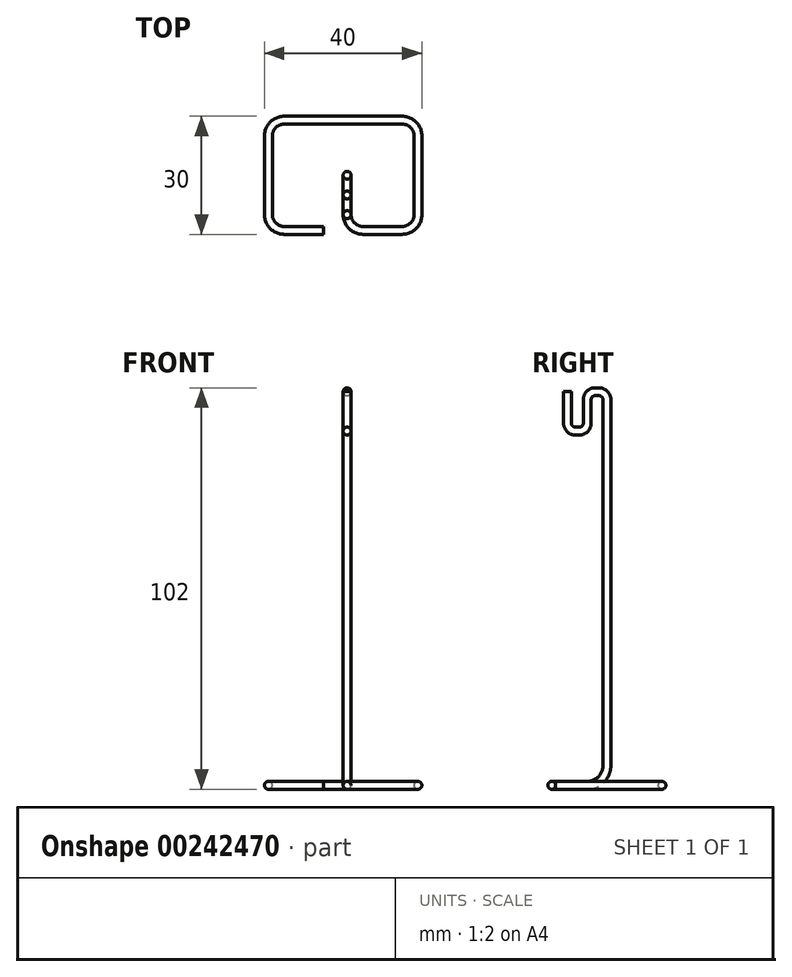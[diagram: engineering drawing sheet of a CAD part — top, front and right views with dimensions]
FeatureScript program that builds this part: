
annotation { "Feature Type Name" : "Feature", "Feature Type Description" : "" }
export const myFeature = defineFeature(function(context is Context, id is Id, definition is map)
    precondition{}
    {
        {
            var Q0;
            Q0=qCreatedBy(makeId("Right.planeOp"),FACE);
            var sketch = newSketch(context, id + "F0", { "sketchPlane" : qUnion([Q0])});
            skLineSegment(sketch, "E0", {"start": v(0, 0) * mm, "end": v(0, 0) * mm});
            skLineSegment(sketch, "E1", {"start": v(5, 5) * mm, "end": v(5, 98) * mm});
            skLineSegment(sketch, "E2", {"start": v(3, 100) * mm, "end": v(2, 100) * mm});
            skLineSegment(sketch, "E3", {"start": v(0, 98) * mm, "end": v(0, 92) * mm});
            skLineSegment(sketch, "E4", {"start": v(-2, 90) * mm, "end": v(-3, 90) * mm});
            skLineSegment(sketch, "E5", {"start": v(-5, 92) * mm, "end": v(-5, 100) * mm});
            skPoint(sketch, "E6.visualSharp", {"position": v(-5, 90) * mm});
            skArc(sketch, "E6.filletArc", {"start": v(-5, 92) * mm, "mid": v(-4.41, 90.59) * mm, "end": v(-3, 90) * mm});
            skPoint(sketch, "E7.visualSharp", {"position": v(0, 90) * mm});
            skArc(sketch, "E7.filletArc", {"start": v(-2, 90) * mm, "mid": v(-0.59, 90.59) * mm, "end": v(0, 92) * mm});
            skPoint(sketch, "E8.visualSharp", {"position": v(0, 100) * mm});
            skArc(sketch, "E8.filletArc", {"start": v(2, 100) * mm, "mid": v(0.59, 99.41) * mm, "end": v(0, 98) * mm});
            skPoint(sketch, "E9.visualSharp", {"position": v(5, 100) * mm});
            skArc(sketch, "E9.filletArc", {"start": v(5, 98) * mm, "mid": v(4.41, 99.41) * mm, "end": v(3, 100) * mm});
            skPoint(sketch, "E10.visualSharp", {"position": v(5, 0) * mm});
            skArc(sketch, "E10.filletArc", {"start": v(0, 0) * mm, "mid": v(3.54, 1.46) * mm, "end": v(5, 5) * mm});
            skPoint(sketch, "E11", {"position": v(-5, 100) * mm});
            skSolve(sketch);
        }
        {
            var Q0;
            Q0=qCreatedBy(makeId("Front.planeOp"),FACE);
            var sketch = newSketch(context, id + "F1", { "sketchPlane" : qUnion([Q0])});
            skCircle(sketch, "E12", {"center": v(1, 0) * mm, "radius": 1 * mm});
            skSolve(sketch);
        }
        {
            var Q0;
            Q0=qCreatedBy(makeId("Top.planeOp"),FACE);
            var sketch = newSketch(context, id + "F2", { "sketchPlane" : qUnion([Q0])});
            skLineSegment(sketch, "E13", {"start": v(0, 0) * mm, "end": v(0, -5) * mm});
            skLineSegment(sketch, "E14", {"start": v(5, -10) * mm, "end": v(15, -10) * mm});
            skLineSegment(sketch, "E15", {"start": v(20, -5) * mm, "end": v(20, 15) * mm});
            skLineSegment(sketch, "E16", {"start": v(15, 20) * mm, "end": v(-15, 20) * mm});
            skLineSegment(sketch, "E17", {"start": v(-20, 15) * mm, "end": v(-20, -5) * mm});
            skLineSegment(sketch, "E18", {"start": v(-15, -10) * mm, "end": v(-5, -10) * mm});
            skPoint(sketch, "E19.visualSharp", {"position": v(-20, -10) * mm});
            skArc(sketch, "E19.filletArc", {"start": v(-20, -5) * mm, "mid": v(-18.54, -8.54) * mm, "end": v(-15, -10) * mm});
            skPoint(sketch, "E20.visualSharp", {"position": v(20, -10) * mm});
            skArc(sketch, "E20.filletArc", {"start": v(15, -10) * mm, "mid": v(18.54, -8.54) * mm, "end": v(20, -5) * mm});
            skPoint(sketch, "E21.visualSharp", {"position": v(20, 20) * mm});
            skArc(sketch, "E21.filletArc", {"start": v(20, 15) * mm, "mid": v(18.54, 18.54) * mm, "end": v(15, 20) * mm});
            skPoint(sketch, "E22.visualSharp", {"position": v(-20, 20) * mm});
            skArc(sketch, "E22.filletArc", {"start": v(-15, 20) * mm, "mid": v(-18.54, 18.54) * mm, "end": v(-20, 15) * mm});
            skPoint(sketch, "E23.visualSharp", {"position": v(0, -10) * mm});
            skArc(sketch, "E23.filletArc", {"start": v(0, -5) * mm, "mid": v(1.46, -8.54) * mm, "end": v(5, -10) * mm});
            skSolve(sketch);
        }
        {
            var Q0;
            Q0=makeQuery(id+"F1.imprint","IMPRINT",FACE,{"disambiguationData":[TD([[makeQuery(id+"F1.imprint","IMPRINT",EDGE,{"derivedFrom":sQuery(id+"F1.wireOp",EDGE,"E12")}),1.0]])]});
            var Q1;
            Q1=sQuery(id+"F0.wireOp",EDGE,"E0");
            var Q2;
            Q2=sQuery(id+"F0.wireOp",EDGE,"E10.filletArc");
            var Q3;
            Q3=sQuery(id+"F0.wireOp",EDGE,"E1");
            var Q4;
            Q4=sQuery(id+"F0.wireOp",EDGE,"E9.filletArc");
            var Q5;
            Q5=sQuery(id+"F0.wireOp",EDGE,"E2");
            var Q6;
            Q6=sQuery(id+"F0.wireOp",EDGE,"E8.filletArc");
            var Q7;
            Q7=sQuery(id+"F0.wireOp",EDGE,"E3");
            var Q8;
            Q8=sQuery(id+"F0.wireOp",EDGE,"E7.filletArc");
            var Q9;
            Q9=sQuery(id+"F0.wireOp",EDGE,"E4");
            var Q10;
            Q10=sQuery(id+"F0.wireOp",EDGE,"E6.filletArc");
            var Q11;
            Q11=sQuery(id+"F0.wireOp",EDGE,"E5");
            sweep(context, id + "F3", {"profiles" : qUnion([Q0]), "path" : qUnion([Q1, Q2, Q3, Q4, Q5, Q6, Q7, Q8, Q9, Q10, Q11])});
        }
        {
            var Q0;
            Q0=makeQuery(id+"F3.opSweep","CAP_FACE",FACE,{"disambiguationData":[OSD([sQuery(id+"F0.wireOp",VERTEX,"E10.filletArc.start"),sQuery(id+"F1.wireOp",EDGE,"E12")])],"isStart":true});
            var Q1;
            Q1=sQuery(id+"F2.wireOp",EDGE,"E13");
            var Q2;
            Q2=sQuery(id+"F2.wireOp",EDGE,"E23.filletArc");
            var Q3;
            Q3=sQuery(id+"F2.wireOp",EDGE,"E14");
            var Q4;
            Q4=sQuery(id+"F2.wireOp",EDGE,"E20.filletArc");
            var Q5;
            Q5=sQuery(id+"F2.wireOp",EDGE,"E15");
            var Q6;
            Q6=sQuery(id+"F2.wireOp",EDGE,"E21.filletArc");
            var Q7;
            Q7=sQuery(id+"F2.wireOp",EDGE,"E16");
            var Q8;
            Q8=sQuery(id+"F2.wireOp",EDGE,"E22.filletArc");
            var Q9;
            Q9=sQuery(id+"F2.wireOp",EDGE,"E17");
            var Q10;
            Q10=sQuery(id+"F2.wireOp",EDGE,"E19.filletArc");
            var Q11;
            Q11=sQuery(id+"F2.wireOp",EDGE,"E18");
            sweep(context, id + "F4", {"operationType" : NewBodyOperationType.ADD, "profiles" : qUnion([Q0]), "path" : qUnion([Q1, Q2, Q3, Q4, Q5, Q6, Q7, Q8, Q9, Q10, Q11])});
        }
    });
